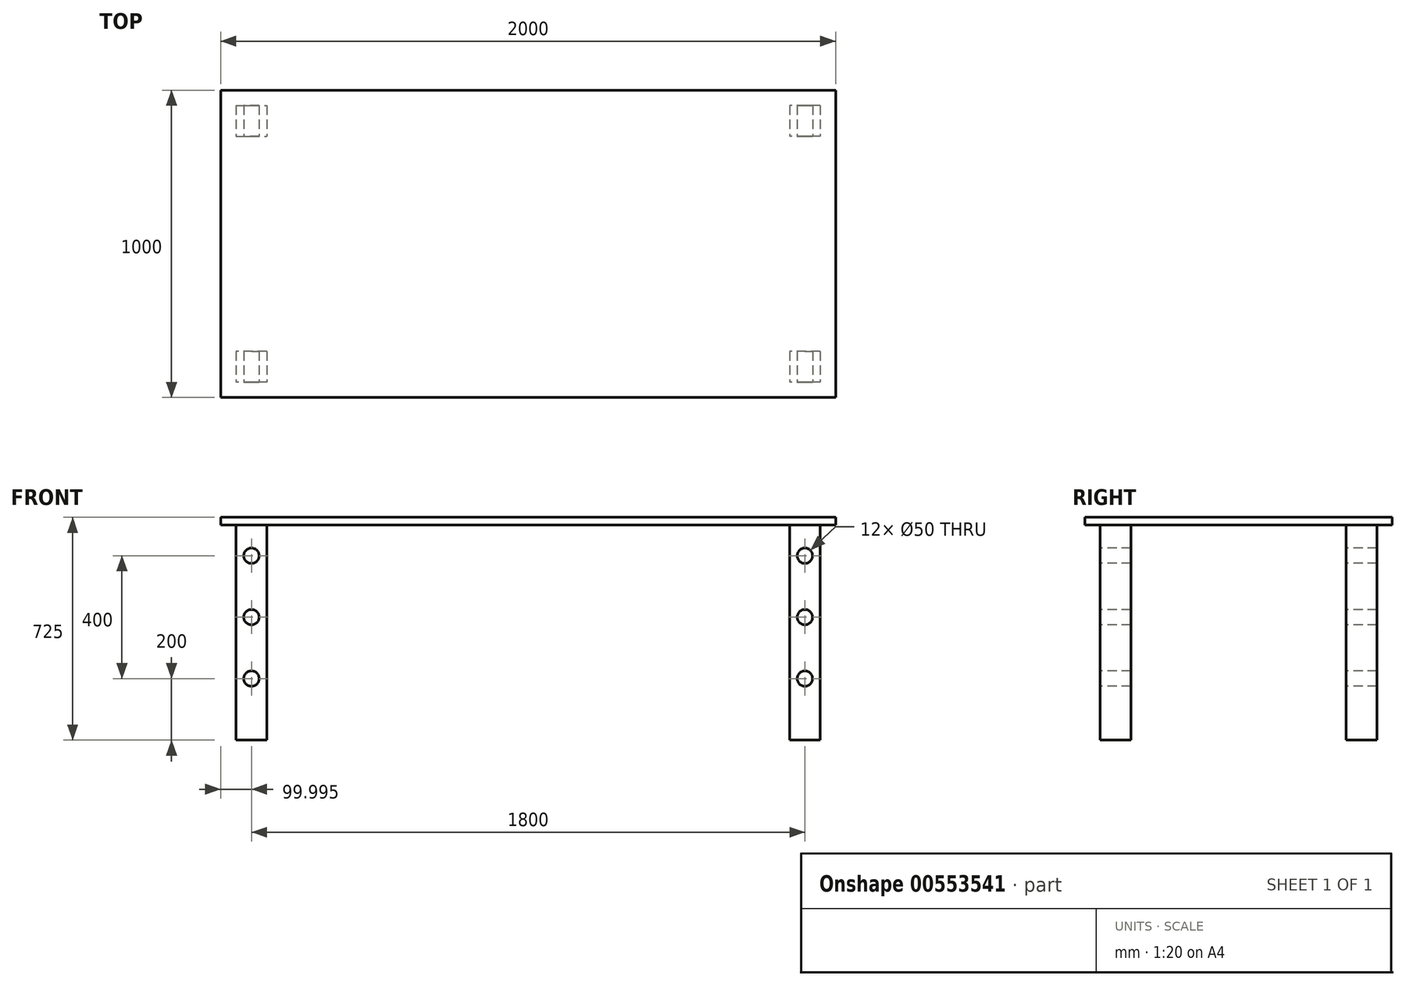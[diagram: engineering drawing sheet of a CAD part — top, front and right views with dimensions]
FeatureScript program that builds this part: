
annotation { "Feature Type Name" : "Feature", "Feature Type Description" : "" }
export const myFeature = defineFeature(function(context is Context, id is Id, definition is map)
    precondition{}
    {
        {
            var Q0;
            Q0=qCreatedBy(makeId("Top.planeOp"),FACE);
            var sketch = newSketch(context, id + "F0", { "sketchPlane" : qUnion([Q0])});
            skLineSegment(sketch, "E0.bottom", {"start": v(-998.28, 496.36) * mm, "end": v(1001.72, 496.36) * mm});
            skLineSegment(sketch, "E0.top", {"start": v(-998.28, -503.64) * mm, "end": v(1001.72, -503.64) * mm});
            skLineSegment(sketch, "E0.left", {"start": v(-998.28, 496.36) * mm, "end": v(-998.28, -503.64) * mm});
            skLineSegment(sketch, "E0.right", {"start": v(1001.72, 496.36) * mm, "end": v(1001.72, -503.64) * mm});
            skSolve(sketch);
        }
        {
            var Q0;
            Q0 = qSketchRegion(id + "F0", true);
            extrude(context, id + "F1", {"entities" : qUnion([Q0]), "depth" : 25 * mm, "offsetDistance" : 25 * mm});
        }
        {
            var Q0;
            Q0=makeQuery(id+"F1.opExtrude","CAP_FACE",FACE,{"disambiguationData":[OSD([sQuery(id+"F0.wireOp",EDGE,"E0.bottom"),sQuery(id+"F0.wireOp",EDGE,"E0.top"),sQuery(id+"F0.wireOp",EDGE,"E0.left"),sQuery(id+"F0.wireOp",EDGE,"E0.right")])],"isStart":true});
            var sketch = newSketch(context, id + "F2", { "sketchPlane" : qUnion([Q0])});
            skLineSegment(sketch, "E1.bottom", {"start": v(-948.28, -446.36) * mm, "end": v(-848.28, -446.36) * mm});
            skLineSegment(sketch, "E1.top", {"start": v(-948.28, -346.36) * mm, "end": v(-848.28, -346.36) * mm});
            skLineSegment(sketch, "E1.left", {"start": v(-948.28, -446.36) * mm, "end": v(-948.28, -346.36) * mm});
            skLineSegment(sketch, "E1.right", {"start": v(-848.28, -446.36) * mm, "end": v(-848.28, -346.36) * mm});
            skLineSegment(sketch, "E2.bottom", {"start": v(-848.28, 353.64) * mm, "end": v(-948.28, 353.64) * mm});
            skLineSegment(sketch, "E2.top", {"start": v(-848.28, 453.64) * mm, "end": v(-948.28, 453.64) * mm});
            skLineSegment(sketch, "E2.left", {"start": v(-848.28, 353.64) * mm, "end": v(-848.28, 453.64) * mm});
            skLineSegment(sketch, "E2.right", {"start": v(-948.28, 353.64) * mm, "end": v(-948.28, 453.64) * mm});
            skLineSegment(sketch, "E3.bottom", {"start": v(951.72, 353.64) * mm, "end": v(851.72, 353.64) * mm});
            skLineSegment(sketch, "E3.top", {"start": v(951.72, 453.64) * mm, "end": v(851.72, 453.64) * mm});
            skLineSegment(sketch, "E3.left", {"start": v(951.72, 353.64) * mm, "end": v(951.72, 453.64) * mm});
            skLineSegment(sketch, "E3.right", {"start": v(851.72, 353.64) * mm, "end": v(851.72, 453.64) * mm});
            skLineSegment(sketch, "E4.bottom", {"start": v(951.72, -446.36) * mm, "end": v(851.72, -446.36) * mm});
            skLineSegment(sketch, "E4.top", {"start": v(951.72, -346.36) * mm, "end": v(851.72, -346.36) * mm});
            skLineSegment(sketch, "E4.left", {"start": v(951.72, -446.36) * mm, "end": v(951.72, -346.36) * mm});
            skLineSegment(sketch, "E4.right", {"start": v(851.72, -446.36) * mm, "end": v(851.72, -346.36) * mm});
            skSolve(sketch);
        }
        {
            var Q0;
            Q0 = qSketchRegion(id + "F2", true);
            extrude(context, id + "F3", {"entities" : qUnion([Q0]), "operationType" : NewBodyOperationType.ADD, "depth" : 700 * mm, "offsetDistance" : 25 * mm});
        }
        {
            var Q0;
            Q0=makeQuery(id+"F3.opExtrude","SWEPT_FACE",FACE,{"disambiguationData":[OSD([sQuery(id+"F2.wireOp",EDGE,"E2.top")])]});
            var sketch = newSketch(context, id + "F4", { "sketchPlane" : qUnion([Q0])});
            skCircle(sketch, "E5", {"center": v(-898.28, -500) * mm, "radius": 25 * mm});
            skCircle(sketch, "E6", {"center": v(-898.28, -300) * mm, "radius": 25 * mm});
            skCircle(sketch, "E7", {"center": v(-898.28, -100) * mm, "radius": 25 * mm});
            skSolve(sketch);
        }
        {
            var Q0;
            Q0=sQuery(id+"F4.wireOp",VERTEX,"E7.center");
            var Q1;
            Q1=sQuery(id+"F4.wireOp",VERTEX,"E6.center");
            var Q2;
            Q2=sQuery(id+"F4.wireOp",VERTEX,"E5.center");
            var Q3;
            Q3=makeQuery(id+"F1.opExtrude","SWEPT_BODY",BODY,{"disambiguationData":[OSD([sQuery(id+"F0.wireOp",EDGE,"E0.bottom"),sQuery(id+"F0.wireOp",EDGE,"E0.top"),sQuery(id+"F0.wireOp",EDGE,"E0.left"),sQuery(id+"F0.wireOp",EDGE,"E0.right")])]});
            hole(context, id + "F5", {"style" : HoleStyle.SIMPLE, "endStyle" : HoleEndStyle.THROUGH, "holeDiameter" : 50 * mm, "isTappedThrough" : true, "tappedDepth" : 12 * mm, "tapClearance" : 3, "locations" : qUnion([Q0, Q1, Q2]), "scope" : qUnion([Q3])});
        }
        {
            var Q0;
            Q0=makeQuery(id+"F3.opExtrude","SWEPT_FACE",FACE,{"disambiguationData":[OSD([sQuery(id+"F2.wireOp",EDGE,"E3.top")])]});
            var sketch = newSketch(context, id + "F6", { "sketchPlane" : qUnion([Q0])});
            skCircle(sketch, "E8", {"center": v(901.72, -500) * mm, "radius": 25 * mm});
            skCircle(sketch, "E9", {"center": v(901.72, -300) * mm, "radius": 25 * mm});
            skCircle(sketch, "E10", {"center": v(901.72, -100) * mm, "radius": 25 * mm});
            skSolve(sketch);
        }
        {
            var Q0;
            Q0=sQuery(id+"F6.wireOp",VERTEX,"E10.center");
            var Q1;
            Q1=sQuery(id+"F6.wireOp",VERTEX,"E9.center");
            var Q2;
            Q2=sQuery(id+"F6.wireOp",VERTEX,"E8.center");
            var Q3;
            Q3=makeQuery(id+"F1.opExtrude","SWEPT_BODY",BODY,{"disambiguationData":[OSD([sQuery(id+"F0.wireOp",EDGE,"E0.bottom"),sQuery(id+"F0.wireOp",EDGE,"E0.top"),sQuery(id+"F0.wireOp",EDGE,"E0.left"),sQuery(id+"F0.wireOp",EDGE,"E0.right")])]});
            hole(context, id + "F7", {"style" : HoleStyle.SIMPLE, "endStyle" : HoleEndStyle.THROUGH, "holeDiameter" : 50 * mm, "isTappedThrough" : true, "tappedDepth" : 12 * mm, "tapClearance" : 3, "locations" : qUnion([Q0, Q1, Q2]), "scope" : qUnion([Q3])});
        }
    });
